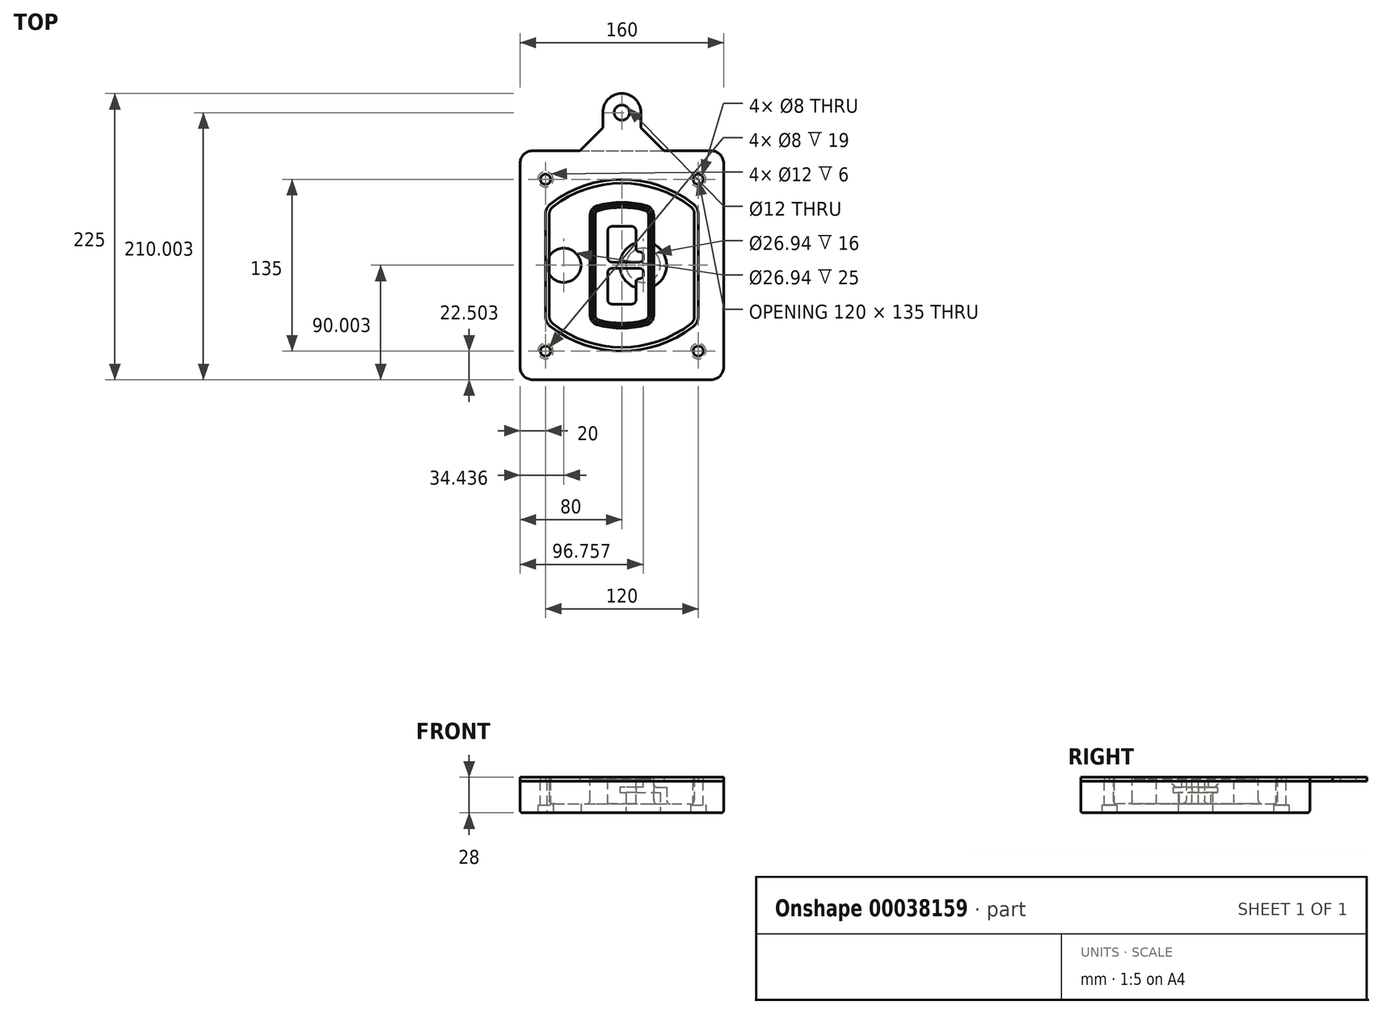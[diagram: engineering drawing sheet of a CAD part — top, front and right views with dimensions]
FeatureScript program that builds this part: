
annotation { "Feature Type Name" : "Feature", "Feature Type Description" : "" }
export const myFeature = defineFeature(function(context is Context, id is Id, definition is map)
    precondition{}
    {
        {
            var Q0;
            Q0=qCreatedBy(makeId("Top.planeOp"),FACE);
            var sketch = newSketch(context, id + "F0", { "sketchPlane" : qUnion([Q0])});
            skPoint(sketch, "E0.rect.middle", {"position": v(0, 0) * mm});
            skLineSegment(sketch, "E1.bottom", {"start": v(24.05, 28.38) * mm, "end": v(164.05, 28.38) * mm});
            skLineSegment(sketch, "E1.top", {"start": v(24.05, 208.38) * mm, "end": v(164.05, 208.38) * mm});
            skLineSegment(sketch, "E1.left", {"start": v(14.05, 38.38) * mm, "end": v(14.05, 198.38) * mm});
            skLineSegment(sketch, "E1.right", {"start": v(174.05, 38.38) * mm, "end": v(174.05, 198.38) * mm});
            skLineSegment(sketch, "E2", {"start": v(14.05, 208.38) * mm, "end": v(174.05, 28.38) * mm, "construction": true});
            skLineSegment(sketch, "E3", {"start": v(174.05, 208.38) * mm, "end": v(14.05, 28.38) * mm, "construction": true});
            skCircle(sketch, "E4", {"center": v(34.05, 185.88) * mm, "radius": 4 * mm});
            skCircle(sketch, "E5", {"center": v(154.05, 185.88) * mm, "radius": 4 * mm});
            skCircle(sketch, "E6", {"center": v(154.05, 50.88) * mm, "radius": 4 * mm});
            skCircle(sketch, "E7", {"center": v(34.05, 50.88) * mm, "radius": 4 * mm});
            skLineSegment(sketch, "E8", {"start": v(34.05, 185.88) * mm, "end": v(154.05, 185.88) * mm, "construction": true});
            skLineSegment(sketch, "E9", {"start": v(154.05, 185.88) * mm, "end": v(154.05, 50.88) * mm, "construction": true});
            skLineSegment(sketch, "E10", {"start": v(154.05, 50.88) * mm, "end": v(34.05, 50.88) * mm, "construction": true});
            skLineSegment(sketch, "E11", {"start": v(34.05, 50.88) * mm, "end": v(34.05, 185.88) * mm, "construction": true});
            skLineSegment(sketch, "E12", {"start": v(34.05, 158.68) * mm, "end": v(34.05, 78.09) * mm});
            skLineSegment(sketch, "E13", {"start": v(154.05, 158.68) * mm, "end": v(154.05, 78.09) * mm});
            skArc(sketch, "E14", {"start": v(150.2, 166.56) * mm, "mid": v(94.05, 185.88) * mm, "end": v(37.9, 166.56) * mm});
            skArc(sketch, "E15", {"start": v(37.9, 70.2) * mm, "mid": v(94.05, 50.88) * mm, "end": v(150.2, 70.2) * mm});
            skLineSegment(sketch, "E16", {"start": v(34.05, 118.38) * mm, "end": v(154.05, 118.38) * mm, "construction": true});
            skPoint(sketch, "E17.visualSharp", {"position": v(34.05, 73.38) * mm});
            skArc(sketch, "E17.filletArc", {"start": v(34.05, 78.09) * mm, "mid": v(35.06, 73.7) * mm, "end": v(37.9, 70.2) * mm});
            skPoint(sketch, "E18.visualSharp", {"position": v(34.05, 163.38) * mm});
            skArc(sketch, "E18.filletArc", {"start": v(37.9, 166.56) * mm, "mid": v(35.06, 163.06) * mm, "end": v(34.05, 158.68) * mm});
            skPoint(sketch, "E19.visualSharp", {"position": v(154.05, 163.38) * mm});
            skArc(sketch, "E19.filletArc", {"start": v(154.05, 158.68) * mm, "mid": v(153.04, 163.06) * mm, "end": v(150.2, 166.56) * mm});
            skPoint(sketch, "E20.visualSharp", {"position": v(154.05, 73.38) * mm});
            skArc(sketch, "E20.filletArc", {"start": v(150.2, 70.2) * mm, "mid": v(153.04, 73.7) * mm, "end": v(154.05, 78.09) * mm});
            skPoint(sketch, "E21.visualSharp", {"position": v(14.05, 208.38) * mm});
            skArc(sketch, "E21.filletArc", {"start": v(24.05, 208.38) * mm, "mid": v(16.98, 205.45) * mm, "end": v(14.05, 198.38) * mm});
            skPoint(sketch, "E22.visualSharp", {"position": v(174.05, 208.38) * mm});
            skArc(sketch, "E22.filletArc", {"start": v(174.05, 198.38) * mm, "mid": v(171.12, 205.45) * mm, "end": v(164.05, 208.38) * mm});
            skPoint(sketch, "E23.visualSharp", {"position": v(174.05, 28.38) * mm});
            skArc(sketch, "E23.filletArc", {"start": v(164.05, 28.38) * mm, "mid": v(171.12, 31.31) * mm, "end": v(174.05, 38.38) * mm});
            skPoint(sketch, "E24.visualSharp", {"position": v(14.05, 28.38) * mm});
            skArc(sketch, "E24.filletArc", {"start": v(14.05, 38.38) * mm, "mid": v(16.98, 31.31) * mm, "end": v(24.05, 28.38) * mm});
            skArc(sketch, "E25.0", {"start": v(151.05, 158.68) * mm, "mid": v(150.34, 161.75) * mm, "end": v(148.36, 164.2) * mm});
            skLineSegment(sketch, "E25.1", {"start": v(151.05, 158.68) * mm, "end": v(151.05, 78.09) * mm});
            skArc(sketch, "E25.2", {"start": v(148.36, 72.57) * mm, "mid": v(150.34, 75.02) * mm, "end": v(151.05, 78.09) * mm});
            skArc(sketch, "E25.3", {"start": v(39.74, 72.57) * mm, "mid": v(94.05, 53.88) * mm, "end": v(148.36, 72.57) * mm});
            skArc(sketch, "E25.4", {"start": v(37.05, 78.09) * mm, "mid": v(37.76, 75.02) * mm, "end": v(39.74, 72.57) * mm});
            skArc(sketch, "E25.5", {"start": v(148.36, 164.2) * mm, "mid": v(94.05, 182.88) * mm, "end": v(39.74, 164.2) * mm});
            skLineSegment(sketch, "E25.6", {"start": v(37.05, 158.68) * mm, "end": v(37.05, 78.09) * mm});
            skArc(sketch, "E25.7", {"start": v(39.74, 164.2) * mm, "mid": v(37.76, 161.75) * mm, "end": v(37.05, 158.68) * mm});
            skArc(sketch, "E26.0", {"start": v(35.43, 169.71) * mm, "mid": v(31.47, 164.82) * mm, "end": v(30.05, 158.68) * mm});
            skArc(sketch, "E26.1", {"start": v(152.67, 169.71) * mm, "mid": v(94.05, 189.88) * mm, "end": v(35.43, 169.71) * mm});
            skArc(sketch, "E26.2", {"start": v(158.05, 158.68) * mm, "mid": v(156.63, 164.82) * mm, "end": v(152.67, 169.71) * mm});
            skLineSegment(sketch, "E26.3", {"start": v(158.05, 158.68) * mm, "end": v(158.05, 78.09) * mm});
            skArc(sketch, "E26.4", {"start": v(152.67, 67.05) * mm, "mid": v(156.63, 71.95) * mm, "end": v(158.05, 78.09) * mm});
            skLineSegment(sketch, "E26.5", {"start": v(30.05, 158.68) * mm, "end": v(30.05, 78.09) * mm});
            skArc(sketch, "E26.6", {"start": v(35.43, 67.05) * mm, "mid": v(94.05, 46.88) * mm, "end": v(152.67, 67.05) * mm});
            skArc(sketch, "E26.7", {"start": v(30.05, 78.09) * mm, "mid": v(31.47, 71.95) * mm, "end": v(35.43, 67.05) * mm});
            skSolve(sketch);
        }
        {
            var Q0;
            Q0=makeQuery(id+"F0.imprint","IMPRINT",FACE,{"disambiguationData":[TD([[makeQuery(id+"F0.imprint","IMPRINT",EDGE,{"derivedFrom":sQuery(id+"F0.wireOp",EDGE,"E1.bottom")}),1.0]])]});
            var Q1;
            Q1=makeQuery(id+"F0.imprint","IMPRINT",FACE,{"disambiguationData":[TD([[makeQuery(id+"F0.imprint","IMPRINT",EDGE,{"derivedFrom":sQuery(id+"F0.wireOp",EDGE,"E12")}),1.0]])]});
            var Q2;
            Q2=makeQuery(id+"F0.imprint","IMPRINT",FACE,{"disambiguationData":[TD([[makeQuery(id+"F0.imprint","IMPRINT",EDGE,{"derivedFrom":sQuery(id+"F0.wireOp",EDGE,"E25.0")}),1.0]])]});
            var Q3;
            Q3=makeQuery(id+"F0.imprint","IMPRINT",FACE,{"disambiguationData":[TD([[makeQuery(id+"F0.imprint","IMPRINT",EDGE,{"derivedFrom":sQuery(id+"F0.wireOp",EDGE,"E12")}),-1.0]])]});
            extrude(context, id + "F1", {"entities" : qUnion([Q0, Q1, Q2, Q3]), "oppositeDirection" : true, "depth" : 25 * mm});
        }
        {
            var Q0;
            Q0=makeQuery(id+"F0.imprint","IMPRINT",FACE,{"disambiguationData":[TD([[makeQuery(id+"F0.imprint","IMPRINT",EDGE,{"derivedFrom":sQuery(id+"F0.wireOp",EDGE,"E12")}),1.0]])]});
            extrude(context, id + "F2", {"entities" : qUnion([Q0]), "operationType" : NewBodyOperationType.ADD, "depth" : 3 * mm});
        }
        {
            var Q0;
            Q0=makeQuery(id+"F0.imprint","IMPRINT",FACE,{"disambiguationData":[TD([[makeQuery(id+"F0.imprint","IMPRINT",EDGE,{"derivedFrom":sQuery(id+"F0.wireOp",EDGE,"E25.0")}),1.0]])]});
            extrude(context, id + "F3", {"entities" : qUnion([Q0]), "operationType" : NewBodyOperationType.REMOVE, "oppositeDirection" : true, "depth" : 18 * mm});
        }
        {
            var Q0;
            Q0=makeQuery(id+"F2.opExtrude","CAP_FACE",FACE,{"disambiguationData":[OSD([sQuery(id+"F0.wireOp",EDGE,"E12"),sQuery(id+"F0.wireOp",EDGE,"E13"),sQuery(id+"F0.wireOp",EDGE,"E14"),sQuery(id+"F0.wireOp",EDGE,"E15"),sQuery(id+"F0.wireOp",EDGE,"E17.filletArc"),sQuery(id+"F0.wireOp",EDGE,"E18.filletArc"),sQuery(id+"F0.wireOp",EDGE,"E19.filletArc"),sQuery(id+"F0.wireOp",EDGE,"E20.filletArc"),sQuery(id+"F0.wireOp",EDGE,"E25.0"),sQuery(id+"F0.wireOp",EDGE,"E25.1"),sQuery(id+"F0.wireOp",EDGE,"E25.2"),sQuery(id+"F0.wireOp",EDGE,"E25.3"),sQuery(id+"F0.wireOp",EDGE,"E25.4"),sQuery(id+"F0.wireOp",EDGE,"E25.5"),sQuery(id+"F0.wireOp",EDGE,"E25.6"),sQuery(id+"F0.wireOp",EDGE,"E25.7")])],"isStart":false});
            var sketch = newSketch(context, id + "F4", { "sketchPlane" : qUnion([Q0])});
            skArc(sketch, "E27.0", {"start": v(74.97, 71.41) * mm, "mid": v(94.05, 68.88) * mm, "end": v(113.13, 71.41) * mm});
            skArc(sketch, "E28.0", {"start": v(113.13, 165.35) * mm, "mid": v(94.05, 167.88) * mm, "end": v(74.97, 165.35) * mm});
            skLineSegment(sketch, "E29", {"start": v(69.05, 157.63) * mm, "end": v(69.05, 79.14) * mm});
            skLineSegment(sketch, "E30", {"start": v(119.05, 157.63) * mm, "end": v(119.05, 79.14) * mm});
            skLineSegment(sketch, "E31", {"start": v(69.05, 163.48) * mm, "end": v(119.05, 163.48) * mm, "construction": true});
            skLineSegment(sketch, "E32", {"start": v(69.05, 73.28) * mm, "end": v(119.05, 73.28) * mm, "construction": true});
            skPoint(sketch, "E33.visualSharp", {"position": v(69.05, 163.48) * mm});
            skArc(sketch, "E33.filletArc", {"start": v(74.97, 165.35) * mm, "mid": v(70.7, 162.5) * mm, "end": v(69.05, 157.63) * mm});
            skPoint(sketch, "E34.visualSharp", {"position": v(119.05, 163.48) * mm});
            skArc(sketch, "E34.filletArc", {"start": v(119.05, 157.63) * mm, "mid": v(117.4, 162.5) * mm, "end": v(113.13, 165.35) * mm});
            skPoint(sketch, "E35.visualSharp", {"position": v(119.05, 73.28) * mm});
            skArc(sketch, "E35.filletArc", {"start": v(113.13, 71.41) * mm, "mid": v(117.4, 74.27) * mm, "end": v(119.05, 79.14) * mm});
            skPoint(sketch, "E36.visualSharp", {"position": v(69.05, 73.28) * mm});
            skArc(sketch, "E36.filletArc", {"start": v(69.05, 79.14) * mm, "mid": v(70.7, 74.27) * mm, "end": v(74.97, 71.41) * mm});
            skArc(sketch, "E37.0", {"start": v(148.36, 164.2) * mm, "mid": v(94.05, 182.88) * mm, "end": v(39.74, 164.2) * mm});
            skArc(sketch, "E37.1", {"start": v(39.74, 164.2) * mm, "mid": v(37.76, 161.75) * mm, "end": v(37.05, 158.68) * mm});
            skLineSegment(sketch, "E37.2", {"start": v(37.05, 158.68) * mm, "end": v(37.05, 78.09) * mm});
            skArc(sketch, "E37.3", {"start": v(37.05, 78.09) * mm, "mid": v(37.76, 75.02) * mm, "end": v(39.74, 72.57) * mm});
            skArc(sketch, "E37.4", {"start": v(39.74, 72.57) * mm, "mid": v(94.05, 53.88) * mm, "end": v(148.36, 72.57) * mm});
            skArc(sketch, "E37.5", {"start": v(148.36, 72.57) * mm, "mid": v(150.34, 75.02) * mm, "end": v(151.05, 78.09) * mm});
            skLineSegment(sketch, "E37.6", {"start": v(151.05, 158.68) * mm, "end": v(151.05, 78.09) * mm});
            skArc(sketch, "E37.7", {"start": v(151.05, 158.68) * mm, "mid": v(150.34, 161.75) * mm, "end": v(148.36, 164.2) * mm});
            skLineSegment(sketch, "E38.0", {"start": v(117.05, 157.63) * mm, "end": v(117.05, 79.14) * mm});
            skArc(sketch, "E38.1", {"start": v(112.61, 73.34) * mm, "mid": v(115.81, 75.49) * mm, "end": v(117.05, 79.14) * mm});
            skArc(sketch, "E38.2", {"start": v(75.49, 73.34) * mm, "mid": v(94.05, 70.88) * mm, "end": v(112.61, 73.34) * mm});
            skArc(sketch, "E38.3", {"start": v(71.05, 79.14) * mm, "mid": v(72.29, 75.49) * mm, "end": v(75.49, 73.34) * mm});
            skLineSegment(sketch, "E38.4", {"start": v(71.05, 157.63) * mm, "end": v(71.05, 79.14) * mm});
            skArc(sketch, "E38.5", {"start": v(117.05, 157.63) * mm, "mid": v(115.81, 161.28) * mm, "end": v(112.61, 163.42) * mm});
            skArc(sketch, "E38.6", {"start": v(75.49, 163.42) * mm, "mid": v(72.29, 161.28) * mm, "end": v(71.05, 157.63) * mm});
            skArc(sketch, "E38.7", {"start": v(112.61, 163.42) * mm, "mid": v(94.05, 165.88) * mm, "end": v(75.49, 163.42) * mm});
            skArc(sketch, "E39.0", {"start": v(115.05, 157.63) * mm, "mid": v(114.23, 160.06) * mm, "end": v(112.1, 161.5) * mm});
            skLineSegment(sketch, "E39.1", {"start": v(115.05, 157.63) * mm, "end": v(115.05, 79.14) * mm});
            skArc(sketch, "E39.2", {"start": v(112.1, 75.27) * mm, "mid": v(114.23, 76.7) * mm, "end": v(115.05, 79.14) * mm});
            skArc(sketch, "E39.3", {"start": v(76, 75.27) * mm, "mid": v(94.05, 72.88) * mm, "end": v(112.1, 75.27) * mm});
            skArc(sketch, "E39.4", {"start": v(73.05, 79.14) * mm, "mid": v(73.87, 76.7) * mm, "end": v(76, 75.27) * mm});
            skArc(sketch, "E39.5", {"start": v(112.1, 161.5) * mm, "mid": v(94.05, 163.88) * mm, "end": v(76, 161.5) * mm});
            skLineSegment(sketch, "E39.6", {"start": v(73.05, 157.63) * mm, "end": v(73.05, 79.14) * mm});
            skArc(sketch, "E39.7", {"start": v(76, 161.5) * mm, "mid": v(73.87, 160.06) * mm, "end": v(73.05, 157.63) * mm});
            skLineSegment(sketch, "E40", {"start": v(69.05, 118.38) * mm, "end": v(119.05, 118.38) * mm, "construction": true});
            skLineSegment(sketch, "E41", {"start": v(83.05, 123.88) * mm, "end": v(83.05, 145.88) * mm});
            skLineSegment(sketch, "E42", {"start": v(86.05, 148.88) * mm, "end": v(102.05, 148.88) * mm});
            skLineSegment(sketch, "E43", {"start": v(105.05, 145.88) * mm, "end": v(105.05, 131.88) * mm});
            skLineSegment(sketch, "E44", {"start": v(108.05, 128.88) * mm, "end": v(108.05, 128.88) * mm});
            skLineSegment(sketch, "E45", {"start": v(111.05, 125.88) * mm, "end": v(111.05, 123.88) * mm});
            skLineSegment(sketch, "E46", {"start": v(108.05, 120.88) * mm, "end": v(86.05, 120.88) * mm});
            skPoint(sketch, "E47.visualSharp", {"position": v(83.05, 148.88) * mm});
            skArc(sketch, "E47.filletArc", {"start": v(86.05, 148.88) * mm, "mid": v(83.93, 148) * mm, "end": v(83.05, 145.88) * mm});
            skPoint(sketch, "E48.visualSharp", {"position": v(105.05, 148.88) * mm});
            skArc(sketch, "E48.filletArc", {"start": v(105.05, 145.88) * mm, "mid": v(104.17, 148) * mm, "end": v(102.05, 148.88) * mm});
            skPoint(sketch, "E49.visualSharp", {"position": v(105.05, 128.88) * mm});
            skArc(sketch, "E49.filletArc", {"start": v(105.05, 131.88) * mm, "mid": v(105.93, 129.76) * mm, "end": v(108.05, 128.88) * mm});
            skPoint(sketch, "E50.visualSharp", {"position": v(111.05, 128.88) * mm});
            skArc(sketch, "E50.filletArc", {"start": v(111.05, 125.88) * mm, "mid": v(110.17, 128) * mm, "end": v(108.05, 128.88) * mm});
            skPoint(sketch, "E51.visualSharp", {"position": v(111.05, 120.88) * mm});
            skArc(sketch, "E51.filletArc", {"start": v(108.05, 120.88) * mm, "mid": v(110.17, 121.76) * mm, "end": v(111.05, 123.88) * mm});
            skPoint(sketch, "E52.visualSharp", {"position": v(83.05, 120.88) * mm});
            skArc(sketch, "E52.filletArc", {"start": v(83.05, 123.88) * mm, "mid": v(83.93, 121.76) * mm, "end": v(86.05, 120.88) * mm});
            skLineSegment(sketch, "E53.0.MirrorCS", {"start": v(108.05, 115.88) * mm, "end": v(86.05, 115.88) * mm});
            skArc(sketch, "E54.0.MirrorCS", {"start": v(83.05, 112.88) * mm, "mid": v(83.93, 115) * mm, "end": v(86.05, 115.88) * mm});
            skLineSegment(sketch, "E55.0.MirrorCS", {"start": v(83.05, 112.88) * mm, "end": v(83.05, 90.88) * mm});
            skArc(sketch, "E56.0.MirrorCS", {"start": v(86.05, 87.88) * mm, "mid": v(83.93, 88.76) * mm, "end": v(83.05, 90.88) * mm});
            skLineSegment(sketch, "E57.0.MirrorCS", {"start": v(86.05, 87.88) * mm, "end": v(102.05, 87.88) * mm});
            skArc(sketch, "E58.0.MirrorCS", {"start": v(105.05, 90.88) * mm, "mid": v(104.17, 88.76) * mm, "end": v(102.05, 87.88) * mm});
            skLineSegment(sketch, "E59.0.MirrorCS", {"start": v(105.05, 90.88) * mm, "end": v(105.05, 104.88) * mm});
            skArc(sketch, "E60.0.MirrorCS", {"start": v(105.05, 104.88) * mm, "mid": v(105.93, 107) * mm, "end": v(108.05, 107.88) * mm});
            skArc(sketch, "E61.0.MirrorCS", {"start": v(111.05, 110.88) * mm, "mid": v(110.17, 108.76) * mm, "end": v(108.05, 107.88) * mm});
            skLineSegment(sketch, "E62.0.MirrorCS", {"start": v(111.05, 110.88) * mm, "end": v(111.05, 112.88) * mm});
            skArc(sketch, "E63.0.MirrorCS", {"start": v(108.05, 115.88) * mm, "mid": v(110.17, 115) * mm, "end": v(111.05, 112.88) * mm});
            skSolve(sketch);
        }
        {
            var Q0;
            Q0=makeQuery(id+"F4.imprint","IMPRINT",FACE,{"disambiguationData":[TD([[makeQuery(id+"F4.imprint","IMPRINT",EDGE,{"derivedFrom":sQuery(id+"F4.wireOp",EDGE,"E27.0")}),1.0]])]});
            var Q1;
            Q1=makeQuery(id+"F4.imprint","IMPRINT",FACE,{"disambiguationData":[TD([[makeQuery(id+"F4.imprint","IMPRINT",EDGE,{"derivedFrom":sQuery(id+"F4.wireOp",EDGE,"E38.0")}),-1.0]])]});
            var Q2;
            Q2=makeQuery(id+"F4.imprint","IMPRINT",FACE,{"disambiguationData":[TD([[makeQuery(id+"F4.imprint","IMPRINT",EDGE,{"derivedFrom":sQuery(id+"F4.wireOp",EDGE,"E39.0")}),1.0]])]});
            extrude(context, id + "F5", {"entities" : qUnion([Q0, Q1, Q2]), "operationType" : NewBodyOperationType.ADD, "endBound" : BoundingType.UP_TO_NEXT, "oppositeDirection" : true, "depth" : 25 * mm});
        }
        {
            var Q0;
            Q0=makeQuery(id+"F4.imprint","IMPRINT",FACE,{"disambiguationData":[TD([[makeQuery(id+"F4.imprint","IMPRINT",EDGE,{"derivedFrom":sQuery(id+"F4.wireOp",EDGE,"E38.0")}),-1.0]])]});
            extrude(context, id + "F6", {"entities" : qUnion([Q0]), "operationType" : NewBodyOperationType.REMOVE, "oppositeDirection" : true, "depth" : 2 * mm});
        }
        {
            var Q0;
            Q0=makeQuery(id+"F1.opExtrude","CAP_FACE",FACE,{"disambiguationData":[OSD([sQuery(id+"F0.wireOp",EDGE,"E1.bottom"),sQuery(id+"F0.wireOp",EDGE,"E1.top"),sQuery(id+"F0.wireOp",EDGE,"E1.left"),sQuery(id+"F0.wireOp",EDGE,"E1.right"),sQuery(id+"F0.wireOp",EDGE,"E4"),sQuery(id+"F0.wireOp",EDGE,"E5"),sQuery(id+"F0.wireOp",EDGE,"E6"),sQuery(id+"F0.wireOp",EDGE,"E7"),sQuery(id+"F0.wireOp",EDGE,"E21.filletArc"),sQuery(id+"F0.wireOp",EDGE,"E22.filletArc"),sQuery(id+"F0.wireOp",EDGE,"E23.filletArc"),sQuery(id+"F0.wireOp",EDGE,"E24.filletArc")])],"isStart":false});
            var sketch = newSketch(context, id + "F7", { "sketchPlane" : qUnion([Q0])});
            skCircle(sketch, "E64", {"center": v(110.8, -118.38) * mm, "radius": 13.47 * mm});
            skCircle(sketch, "E65", {"center": v(48.49, -118.38) * mm, "radius": 13.47 * mm});
            skLineSegment(sketch, "E66", {"start": v(174.05, -118.38) * mm, "end": v(14.05, -118.38) * mm});
            skCircle(sketch, "E67", {"center": v(110.8, -118.38) * mm, "radius": 18.47 * mm});
            skCircle(sketch, "E68", {"center": v(154.05, -185.88) * mm, "radius": 6 * mm});
            skCircle(sketch, "E69", {"center": v(34.05, -185.88) * mm, "radius": 6 * mm});
            skCircle(sketch, "E70", {"center": v(34.05, -50.88) * mm, "radius": 6 * mm});
            skCircle(sketch, "E71", {"center": v(154.05, -50.88) * mm, "radius": 6 * mm});
            skSolve(sketch);
        }
        {
            var Q0;
            {var subQ1=sQuery(id+"F7.wireOp",EDGE,"E66");var subQ4=sQuery(id+"F7.wireOp",EDGE,"E64");var subQ6=makeQuery(id+"F7.imprint","INTERSECT",VERTEX,{"disambiguationData":[OD(0.0)],"derivedFrom":[subQ4,subQ1]});Q0=makeQuery(id+"F7.imprint","IMPRINT",FACE,{"disambiguationData":[TD([[makeQuery(id+"F7.imprint","IMPRINT",EDGE,{"disambiguationData":[TD([[subQ6,-1.0]])],"derivedFrom":subQ4}),-1.0]])]});}
            var Q1;
            {var subQ0=sQuery(id+"F7.wireOp",EDGE,"E66");var subQ1=sQuery(id+"F7.wireOp",EDGE,"E64");var subQ3=makeQuery(id+"F7.imprint","INTERSECT",VERTEX,{"disambiguationData":[OD(0.0)],"derivedFrom":[subQ1,subQ0]});Q1=makeQuery(id+"F7.imprint","IMPRINT",FACE,{"disambiguationData":[TD([[makeQuery(id+"F7.imprint","IMPRINT",EDGE,{"disambiguationData":[TD([[subQ3,-1.0]])],"derivedFrom":subQ1}),1.0]])]});}
            var Q2;
            {var subQ0=sQuery(id+"F7.wireOp",EDGE,"E66");var subQ1=sQuery(id+"F7.wireOp",EDGE,"E64");var subQ3=makeQuery(id+"F7.imprint","INTERSECT",VERTEX,{"disambiguationData":[OD(0.0)],"derivedFrom":[subQ1,subQ0]});Q2=makeQuery(id+"F7.imprint","IMPRINT",FACE,{"disambiguationData":[TD([[makeQuery(id+"F7.imprint","IMPRINT",EDGE,{"disambiguationData":[TD([[subQ3,1.0]])],"derivedFrom":subQ1}),1.0]])]});}
            var Q3;
            {var subQ1=sQuery(id+"F7.wireOp",EDGE,"E66");var subQ4=sQuery(id+"F7.wireOp",EDGE,"E64");var subQ6=makeQuery(id+"F7.imprint","INTERSECT",VERTEX,{"disambiguationData":[OD(0.0)],"derivedFrom":[subQ4,subQ1]});Q3=makeQuery(id+"F7.imprint","IMPRINT",FACE,{"disambiguationData":[TD([[makeQuery(id+"F7.imprint","IMPRINT",EDGE,{"disambiguationData":[TD([[subQ6,1.0]])],"derivedFrom":subQ4}),-1.0]])]});}
            extrude(context, id + "F8", {"entities" : qUnion([Q0, Q1, Q2, Q3]), "operationType" : NewBodyOperationType.ADD, "oppositeDirection" : true, "depth" : 20 * mm});
        }
        {
            var Q0;
            {var subQ0=sQuery(id+"F7.wireOp",EDGE,"E66");var subQ1=sQuery(id+"F7.wireOp",EDGE,"E64");var subQ3=makeQuery(id+"F7.imprint","INTERSECT",VERTEX,{"disambiguationData":[OD(0.0)],"derivedFrom":[subQ1,subQ0]});Q0=makeQuery(id+"F7.imprint","IMPRINT",FACE,{"disambiguationData":[TD([[makeQuery(id+"F7.imprint","IMPRINT",EDGE,{"disambiguationData":[TD([[subQ3,-1.0]])],"derivedFrom":subQ1}),1.0]])]});}
            var Q1;
            {var subQ0=sQuery(id+"F7.wireOp",EDGE,"E66");var subQ1=sQuery(id+"F7.wireOp",EDGE,"E64");var subQ3=makeQuery(id+"F7.imprint","INTERSECT",VERTEX,{"disambiguationData":[OD(0.0)],"derivedFrom":[subQ1,subQ0]});Q1=makeQuery(id+"F7.imprint","IMPRINT",FACE,{"disambiguationData":[TD([[makeQuery(id+"F7.imprint","IMPRINT",EDGE,{"disambiguationData":[TD([[subQ3,1.0]])],"derivedFrom":subQ1}),1.0]])]});}
            extrude(context, id + "F9", {"entities" : qUnion([Q0, Q1]), "operationType" : NewBodyOperationType.REMOVE, "oppositeDirection" : true, "depth" : 16 * mm});
        }
        {
            var Q0;
            {var subQ0=sQuery(id+"F7.wireOp",EDGE,"E66");var subQ1=sQuery(id+"F7.wireOp",EDGE,"E65");var subQ3=makeQuery(id+"F7.imprint","INTERSECT",VERTEX,{"disambiguationData":[OD(0.0)],"derivedFrom":[subQ1,subQ0]});Q0=makeQuery(id+"F7.imprint","IMPRINT",FACE,{"disambiguationData":[TD([[makeQuery(id+"F7.imprint","IMPRINT",EDGE,{"disambiguationData":[TD([[subQ3,-1.0]])],"derivedFrom":subQ1}),1.0]])]});}
            var Q1;
            {var subQ0=sQuery(id+"F7.wireOp",EDGE,"E66");var subQ1=sQuery(id+"F7.wireOp",EDGE,"E65");var subQ3=makeQuery(id+"F7.imprint","INTERSECT",VERTEX,{"disambiguationData":[OD(0.0)],"derivedFrom":[subQ1,subQ0]});Q1=makeQuery(id+"F7.imprint","IMPRINT",FACE,{"disambiguationData":[TD([[makeQuery(id+"F7.imprint","IMPRINT",EDGE,{"disambiguationData":[TD([[subQ3,1.0]])],"derivedFrom":subQ1}),1.0]])]});}
            extrude(context, id + "F10", {"entities" : qUnion([Q0, Q1]), "operationType" : NewBodyOperationType.REMOVE, "oppositeDirection" : true, "depth" : 25 * mm});
        }
        {
            var Q0;
            Q0=makeQuery(id+"F7.imprint","IMPRINT",FACE,{"disambiguationData":[TD([[makeQuery(id+"F7.imprint","IMPRINT",EDGE,{"derivedFrom":sQuery(id+"F7.wireOp",EDGE,"E68")}),1.0]])]});
            var Q1;
            Q1=makeQuery(id+"F7.imprint","IMPRINT",FACE,{"disambiguationData":[TD([[makeQuery(id+"F7.imprint","IMPRINT",EDGE,{"derivedFrom":makeQuery(id+"F1.opExtrude","CAP_EDGE",EDGE,{"disambiguationData":[OSD([sQuery(id+"F0.wireOp",EDGE,"E5")])],"isStart":false})}),-1.0]])]});
            var Q2;
            Q2=makeQuery(id+"F7.imprint","IMPRINT",FACE,{"disambiguationData":[TD([[makeQuery(id+"F7.imprint","IMPRINT",EDGE,{"derivedFrom":sQuery(id+"F7.wireOp",EDGE,"E69")}),1.0]])]});
            var Q3;
            Q3=makeQuery(id+"F7.imprint","IMPRINT",FACE,{"disambiguationData":[TD([[makeQuery(id+"F7.imprint","IMPRINT",EDGE,{"derivedFrom":makeQuery(id+"F1.opExtrude","CAP_EDGE",EDGE,{"disambiguationData":[OSD([sQuery(id+"F0.wireOp",EDGE,"E4")])],"isStart":false})}),-1.0]])]});
            var Q4;
            Q4=makeQuery(id+"F7.imprint","IMPRINT",FACE,{"disambiguationData":[TD([[makeQuery(id+"F7.imprint","IMPRINT",EDGE,{"derivedFrom":sQuery(id+"F7.wireOp",EDGE,"E70")}),1.0]])]});
            var Q5;
            Q5=makeQuery(id+"F7.imprint","IMPRINT",FACE,{"disambiguationData":[TD([[makeQuery(id+"F7.imprint","IMPRINT",EDGE,{"derivedFrom":makeQuery(id+"F1.opExtrude","CAP_EDGE",EDGE,{"disambiguationData":[OSD([sQuery(id+"F0.wireOp",EDGE,"E7")])],"isStart":false})}),-1.0]])]});
            var Q6;
            Q6=makeQuery(id+"F7.imprint","IMPRINT",FACE,{"disambiguationData":[TD([[makeQuery(id+"F7.imprint","IMPRINT",EDGE,{"derivedFrom":sQuery(id+"F7.wireOp",EDGE,"E71")}),1.0]])]});
            var Q7;
            Q7=makeQuery(id+"F7.imprint","IMPRINT",FACE,{"disambiguationData":[TD([[makeQuery(id+"F7.imprint","IMPRINT",EDGE,{"derivedFrom":makeQuery(id+"F1.opExtrude","CAP_EDGE",EDGE,{"disambiguationData":[OSD([sQuery(id+"F0.wireOp",EDGE,"E6")])],"isStart":false})}),-1.0]])]});
            extrude(context, id + "F11", {"entities" : qUnion([Q0, Q1, Q2, Q3, Q4, Q5, Q6, Q7]), "operationType" : NewBodyOperationType.REMOVE, "oppositeDirection" : true, "depth" : 6 * mm});
        }
        {
            var Q0;
            Q0=makeQuery(id+"F9.boolean.opBoolean","COPY",FACE,{"derivedFrom":makeQuery(id+"F9.opExtrude","CAP_FACE",FACE,{"disambiguationData":[OSD([sQuery(id+"F7.wireOp",EDGE,"E64")])],"isStart":false})});
            var sketch = newSketch(context, id + "F12", { "sketchPlane" : qUnion([Q0])});
            skArc(sketch, "E72.0", {"start": v(105.05, -100.83) * mm, "mid": v(96.62, -106.56) * mm, "end": v(92.5, -115.88) * mm});
            skArc(sketch, "E72.1", {"start": v(92.5, -120.88) * mm, "mid": v(96.62, -130.2) * mm, "end": v(105.05, -135.93) * mm});
            skLineSegment(sketch, "E73", {"start": v(92.5, -120.88) * mm, "end": v(108.05, -120.88) * mm});
            skLineSegment(sketch, "E74.0", {"start": v(108.05, -115.88) * mm, "end": v(92.5, -115.88) * mm});
            skArc(sketch, "E74.1", {"start": v(108.05, -115.88) * mm, "mid": v(110.17, -115) * mm, "end": v(111.05, -112.88) * mm});
            skLineSegment(sketch, "E74.2", {"start": v(111.05, -110.88) * mm, "end": v(111.05, -112.88) * mm});
            skArc(sketch, "E74.3", {"start": v(111.05, -110.88) * mm, "mid": v(110.17, -108.76) * mm, "end": v(108.05, -107.88) * mm});
            skArc(sketch, "E74.4", {"start": v(105.05, -104.88) * mm, "mid": v(105.93, -107) * mm, "end": v(108.05, -107.88) * mm});
            skLineSegment(sketch, "E74.5", {"start": v(105.05, -100.83) * mm, "end": v(105.05, -104.88) * mm});
            skLineSegment(sketch, "E74.7", {"start": v(108.05, -120.88) * mm, "end": v(92.5, -120.88) * mm});
            skArc(sketch, "E74.8", {"start": v(108.05, -120.88) * mm, "mid": v(110.17, -121.76) * mm, "end": v(111.05, -123.88) * mm});
            skLineSegment(sketch, "E74.9", {"start": v(111.05, -125.88) * mm, "end": v(111.05, -123.88) * mm});
            skArc(sketch, "E74.10", {"start": v(111.05, -125.88) * mm, "mid": v(110.17, -128) * mm, "end": v(108.05, -128.88) * mm});
            skArc(sketch, "E74.11", {"start": v(105.05, -131.88) * mm, "mid": v(105.93, -129.76) * mm, "end": v(108.05, -128.88) * mm});
            skLineSegment(sketch, "E74.12", {"start": v(105.05, -135.93) * mm, "end": v(105.05, -131.88) * mm});
            skPoint(sketch, "E75.orphan", {"position": v(105.05, -145.88) * mm});
            skPoint(sketch, "E76.orphan", {"position": v(86.05, -120.88) * mm});
            skPoint(sketch, "E77.orphan", {"position": v(86.05, -115.88) * mm});
            skPoint(sketch, "E78.orphan", {"position": v(105.05, -90.88) * mm});
            skSolve(sketch);
        }
        {
            var Q0;
            {var subQ7=sQuery(id+"F12.wireOp",EDGE,"E72.0");var subQ14=sQuery(id+"F12.wireOp",EDGE,"E72.1");var subQ16=sQuery(id+"F12.wireOp",EDGE,"E74.1");var subQ18=sQuery(id+"F12.wireOp",EDGE,"E74.8");Q0=qUnion([makeQuery(id+"F12.imprint","IMPRINT",FACE,{"disambiguationData":[TD([[makeQuery(id+"F12.imprint","IMPRINT",EDGE,{"derivedFrom":subQ7}),1.0]])]}),makeQuery(id+"F12.imprint","IMPRINT",FACE,{"disambiguationData":[TD([[makeQuery(id+"F12.imprint","IMPRINT",EDGE,{"derivedFrom":subQ14}),1.0]])]}),makeQuery(id+"F12.imprint","IMPRINT",FACE,{"disambiguationData":[TD([[makeQuery(id+"F12.imprint","IMPRINT",EDGE,{"derivedFrom":subQ16}),1.0]])]}),makeQuery(id+"F12.imprint","IMPRINT",FACE,{"disambiguationData":[TD([[makeQuery(id+"F12.imprint","IMPRINT",EDGE,{"derivedFrom":subQ18}),-1.0]])]})]);}
            var Q1;
            Q1=makeQuery(id+"F5.boolean.opBoolean","SPLIT",FACE,{"disambiguationData":[TD([makeQuery(id+"F5.opExtrude","SWEPT_FACE",FACE,{"disambiguationData":[OSD([sQuery(id+"F4.wireOp",EDGE,"E41")])]})])],"derivedFrom":makeQuery(id+"F3.boolean.opBoolean","COPY",FACE,{"derivedFrom":makeQuery(id+"F3.opExtrude","CAP_FACE",FACE,{"disambiguationData":[OSD([sQuery(id+"F0.wireOp",EDGE,"E25.0"),sQuery(id+"F0.wireOp",EDGE,"E25.1"),sQuery(id+"F0.wireOp",EDGE,"E25.2"),sQuery(id+"F0.wireOp",EDGE,"E25.3"),sQuery(id+"F0.wireOp",EDGE,"E25.4"),sQuery(id+"F0.wireOp",EDGE,"E25.5"),sQuery(id+"F0.wireOp",EDGE,"E25.6"),sQuery(id+"F0.wireOp",EDGE,"E25.7")])],"isStart":false})})});
            extrude(context, id + "F13", {"entities" : qUnion([Q0]), "operationType" : NewBodyOperationType.REMOVE, "endBound" : BoundingType.UP_TO_SURFACE, "endBoundEntityFace" : qUnion([Q1]), "depth" : 25 * mm});
        }
        {
            var Q0;
            Q0=makeQuery(id+"F3.boolean.opBoolean","COPY",EDGE,{"derivedFrom":makeQuery(id+"F3.opExtrude","CAP_EDGE",EDGE,{"disambiguationData":[OSD([sQuery(id+"F0.wireOp",EDGE,"E25.6")])],"isStart":false})});
            var Q1;
            Q1=makeQuery(id+"F8.boolean.opBoolean","INTERSECT",EDGE,{"derivedFrom":[makeQuery(id+"F5.opExtrude","SWEPT_FACE",FACE,{"disambiguationData":[OSD([sQuery(id+"F4.wireOp",EDGE,"E30")])]}),makeQuery(id+"F8.opExtrude","CAP_FACE",FACE,{"disambiguationData":[OSD([sQuery(id+"F7.wireOp",EDGE,"E67")])],"isStart":false})]});
            var Q2;
            Q2=makeQuery(id+"F8.boolean.opBoolean","INTERSECT",EDGE,{"disambiguationData":[OD(1.0)],"derivedFrom":[makeQuery(id+"F5.opExtrude","SWEPT_FACE",FACE,{"disambiguationData":[OSD([sQuery(id+"F4.wireOp",EDGE,"E30")])]}),makeQuery(id+"F8.opExtrude","SWEPT_FACE",FACE,{"disambiguationData":[OSD([sQuery(id+"F7.wireOp",EDGE,"E67")])]})]});
            var Q3;
            {var subQ0=sQuery(id+"F4.wireOp",EDGE,"E30");Q3=makeQuery(id+"F8.boolean.opBoolean","SPLIT",EDGE,{"disambiguationData":[TD([makeQuery(id+"F5.opExtrude","SWEPT_FACE",FACE,{"disambiguationData":[OSD([sQuery(id+"F4.wireOp",EDGE,"E35.filletArc")])]})])],"derivedFrom":makeQuery(id+"F5.opExtrude","CAP_EDGE",EDGE,{"disambiguationData":[OSD([subQ0])],"isStart":false})});}
            var Q4;
            {var subQ0=sQuery(id+"F0.wireOp",EDGE,"E25.7");var subQ1=sQuery(id+"F0.wireOp",EDGE,"E25.1");var subQ2=sQuery(id+"F0.wireOp",EDGE,"E25.6");var subQ3=sQuery(id+"F0.wireOp",EDGE,"E25.5");var subQ4=sQuery(id+"F0.wireOp",EDGE,"E25.4");var subQ5=sQuery(id+"F0.wireOp",EDGE,"E25.0");var subQ6=sQuery(id+"F0.wireOp",EDGE,"E25.2");var subQ7=sQuery(id+"F0.wireOp",EDGE,"E25.3");Q4=makeQuery(id+"F8.boolean.opBoolean","INTERSECT",EDGE,{"derivedFrom":[makeQuery(id+"F5.boolean.opBoolean","SPLIT",FACE,{"disambiguationData":[TD([makeQuery(id+"F2.opExtrude","SWEPT_FACE",FACE,{"disambiguationData":[OSD([subQ5])]})])],"derivedFrom":makeQuery(id+"F3.boolean.opBoolean","COPY",FACE,{"derivedFrom":makeQuery(id+"F3.opExtrude","CAP_FACE",FACE,{"disambiguationData":[OSD([subQ5,subQ1,subQ6,subQ7,subQ4,subQ3,subQ2,subQ0])],"isStart":false})})}),makeQuery(id+"F8.opExtrude","SWEPT_FACE",FACE,{"disambiguationData":[OSD([sQuery(id+"F7.wireOp",EDGE,"E67")])]})]});}
            var Q5;
            Q5=makeQuery(id+"F8.boolean.opBoolean","INTERSECT",EDGE,{"disambiguationData":[OD(0.0)],"derivedFrom":[makeQuery(id+"F5.opExtrude","SWEPT_FACE",FACE,{"disambiguationData":[OSD([sQuery(id+"F4.wireOp",EDGE,"E30")])]}),makeQuery(id+"F8.opExtrude","SWEPT_FACE",FACE,{"disambiguationData":[OSD([sQuery(id+"F7.wireOp",EDGE,"E67")])]})]});
            fillet(context, id + "F14", {"entities" : qUnion([Q0, Q1, Q2, Q3, Q4, Q5]), "radius" : 3 * mm, "tangentPropagation" : true, "allowEdgeOverflow" : false});
        }
        {
            var Q0;
            Q0=makeQuery(id+"F1.opExtrude","CAP_EDGE",EDGE,{"disambiguationData":[OSD([sQuery(id+"F0.wireOp",EDGE,"E1.bottom")])],"isStart":false});
            fillet(context, id + "F15", {"entities" : qUnion([Q0]), "radius" : 2 * mm, "tangentPropagation" : true, "allowEdgeOverflow" : false});
        }
        {
            var Q0;
            {var subQ0=sQuery(id+"F0.wireOp",EDGE,"E1.bottom");var subQ1=sQuery(id+"F0.wireOp",EDGE,"E1.top");var subQ2=sQuery(id+"F0.wireOp",EDGE,"E1.left");var subQ3=sQuery(id+"F0.wireOp",EDGE,"E1.right");var subQ4=sQuery(id+"F0.wireOp",EDGE,"E4");var subQ5=sQuery(id+"F0.wireOp",EDGE,"E5");var subQ6=sQuery(id+"F0.wireOp",EDGE,"E6");var subQ7=sQuery(id+"F0.wireOp",EDGE,"E7");var subQ8=sQuery(id+"F0.wireOp",EDGE,"E21.filletArc");var subQ9=sQuery(id+"F0.wireOp",EDGE,"E22.filletArc");var subQ10=sQuery(id+"F0.wireOp",EDGE,"E23.filletArc");var subQ11=sQuery(id+"F0.wireOp",EDGE,"E24.filletArc");Q0=makeQuery(id+"F2.boolean.opBoolean","SPLIT",FACE,{"disambiguationData":[TD([makeQuery(id+"F1.opExtrude","SWEPT_FACE",FACE,{"disambiguationData":[OSD([subQ0])]})])],"derivedFrom":makeQuery(id+"F1.opExtrude","CAP_FACE",FACE,{"disambiguationData":[OSD([subQ0,subQ1,subQ2,subQ3,subQ4,subQ5,subQ6,subQ7,subQ8,subQ9,subQ10,subQ11])],"isStart":true})});}
            var sketch = newSketch(context, id + "F16", { "sketchPlane" : qUnion([Q0])});
            skLineSegment(sketch, "E79.0", {"start": v(24.05, 208.38) * mm, "end": v(164.05, 208.38) * mm});
            skArc(sketch, "E79.1", {"start": v(24.05, 208.38) * mm, "mid": v(16.98, 205.45) * mm, "end": v(14.05, 198.38) * mm});
            skLineSegment(sketch, "E79.2", {"start": v(14.05, 38.38) * mm, "end": v(14.05, 198.38) * mm});
            skArc(sketch, "E79.3", {"start": v(14.05, 38.38) * mm, "mid": v(16.98, 31.31) * mm, "end": v(24.05, 28.38) * mm});
            skLineSegment(sketch, "E79.4", {"start": v(24.05, 28.38) * mm, "end": v(164.05, 28.38) * mm});
            skArc(sketch, "E79.5", {"start": v(164.05, 28.38) * mm, "mid": v(171.12, 31.31) * mm, "end": v(174.05, 38.38) * mm});
            skLineSegment(sketch, "E79.6", {"start": v(174.05, 38.38) * mm, "end": v(174.05, 198.38) * mm});
            skArc(sketch, "E79.7", {"start": v(174.05, 198.38) * mm, "mid": v(171.12, 205.45) * mm, "end": v(164.05, 208.38) * mm});
            skCircle(sketch, "E79.8", {"center": v(154.05, 185.88) * mm, "radius": 4 * mm});
            skCircle(sketch, "E79.9", {"center": v(34.05, 185.88) * mm, "radius": 4 * mm});
            skCircle(sketch, "E79.10", {"center": v(34.05, 50.88) * mm, "radius": 4 * mm});
            skCircle(sketch, "E79.11", {"center": v(154.05, 50.88) * mm, "radius": 4 * mm});
            skCircle(sketch, "E80", {"center": v(94.05, 238.38) * mm, "radius": 6 * mm});
            skLineSegment(sketch, "E81", {"start": v(79.05, 238.38) * mm, "end": v(79.05, 226.38) * mm});
            skLineSegment(sketch, "E82", {"start": v(109.05, 238.38) * mm, "end": v(109.05, 226.38) * mm});
            skArc(sketch, "E83", {"start": v(109.05, 238.38) * mm, "mid": v(94.05, 253.38) * mm, "end": v(79.05, 238.38) * mm});
            skLineSegment(sketch, "E84", {"start": v(94.05, 238.38) * mm, "end": v(94.05, 208.38) * mm, "construction": true});
            skLineSegment(sketch, "E85", {"start": v(79.05, 226.38) * mm, "end": v(61.05, 208.38) * mm});
            skLineSegment(sketch, "E86", {"start": v(109.05, 226.38) * mm, "end": v(127.05, 208.38) * mm});
            skLineSegment(sketch, "E87", {"start": v(14.05, 118.38) * mm, "end": v(174.05, 118.38) * mm, "construction": true});
            skLineSegment(sketch, "E88.MirrorCS", {"start": v(24.05, -151.62) * mm, "end": v(164.05, -151.62) * mm});
            skLineSegment(sketch, "E89.MirrorCS", {"start": v(79.05, -1.62) * mm, "end": v(79.05, 10.38) * mm});
            skLineSegment(sketch, "E90.MirrorCS", {"start": v(109.05, -1.62) * mm, "end": v(109.05, 10.38) * mm});
            skCircle(sketch, "E91.MirrorC", {"center": v(94.05, -1.62) * mm, "radius": 6 * mm});
            skArc(sketch, "E92.MirrorCS", {"start": v(109.05, -1.62) * mm, "mid": v(94.05, -16.62) * mm, "end": v(79.05, -1.62) * mm});
            skLineSegment(sketch, "E93.MirrorCS", {"start": v(109.05, 10.38) * mm, "end": v(127.05, 28.38) * mm});
            skLineSegment(sketch, "E94.MirrorCS", {"start": v(79.05, 10.38) * mm, "end": v(61.05, 28.38) * mm});
            skLineSegment(sketch, "E95.MirrorCS", {"start": v(94.05, -1.62) * mm, "end": v(94.05, 28.38) * mm});
            skSolve(sketch);
        }
        {
            var Q0;
            Q0=makeQuery(id+"F16.imprint","IMPRINT",FACE,{"disambiguationData":[TD([[makeQuery(id+"F16.imprint","IMPRINT",EDGE,{"derivedFrom":sQuery(id+"F16.wireOp",EDGE,"E80")}),-1.0]])]});
            var Q1;
            Q1=makeQuery(id+"F16.imprint","IMPRINT",FACE,{"disambiguationData":[TD([[makeQuery(id+"F16.imprint","IMPRINT",EDGE,{"derivedFrom":sQuery(id+"F16.wireOp",EDGE,"E92.MirrorCS")}),-1.0]])]});
            var Q2;
            {var subQ7=sQuery(id+"F16.wireOp",EDGE,"E79.1");Q2=makeQuery(id+"F16.imprint","IMPRINT",FACE,{"disambiguationData":[TD([[makeQuery(id+"F16.imprint","IMPRINT",EDGE,{"derivedFrom":subQ7}),1.0]])]});}
            var Q3;
            Q3=makeQuery(id+"F2.opExtrude","CAP_FACE",FACE,{"disambiguationData":[OSD([sQuery(id+"F0.wireOp",EDGE,"E12"),sQuery(id+"F0.wireOp",EDGE,"E13"),sQuery(id+"F0.wireOp",EDGE,"E14"),sQuery(id+"F0.wireOp",EDGE,"E15"),sQuery(id+"F0.wireOp",EDGE,"E17.filletArc"),sQuery(id+"F0.wireOp",EDGE,"E18.filletArc"),sQuery(id+"F0.wireOp",EDGE,"E19.filletArc"),sQuery(id+"F0.wireOp",EDGE,"E20.filletArc"),sQuery(id+"F0.wireOp",EDGE,"E25.0"),sQuery(id+"F0.wireOp",EDGE,"E25.1"),sQuery(id+"F0.wireOp",EDGE,"E25.2"),sQuery(id+"F0.wireOp",EDGE,"E25.3"),sQuery(id+"F0.wireOp",EDGE,"E25.4"),sQuery(id+"F0.wireOp",EDGE,"E25.5"),sQuery(id+"F0.wireOp",EDGE,"E25.6"),sQuery(id+"F0.wireOp",EDGE,"E25.7")])],"isStart":false});
            extrude(context, id + "F17", {"entities" : qUnion([Q0, Q1, Q2]), "endBound" : BoundingType.UP_TO_SURFACE, "endBoundEntityFace" : qUnion([Q3]), "depth" : 25 * mm});
        }
    });
